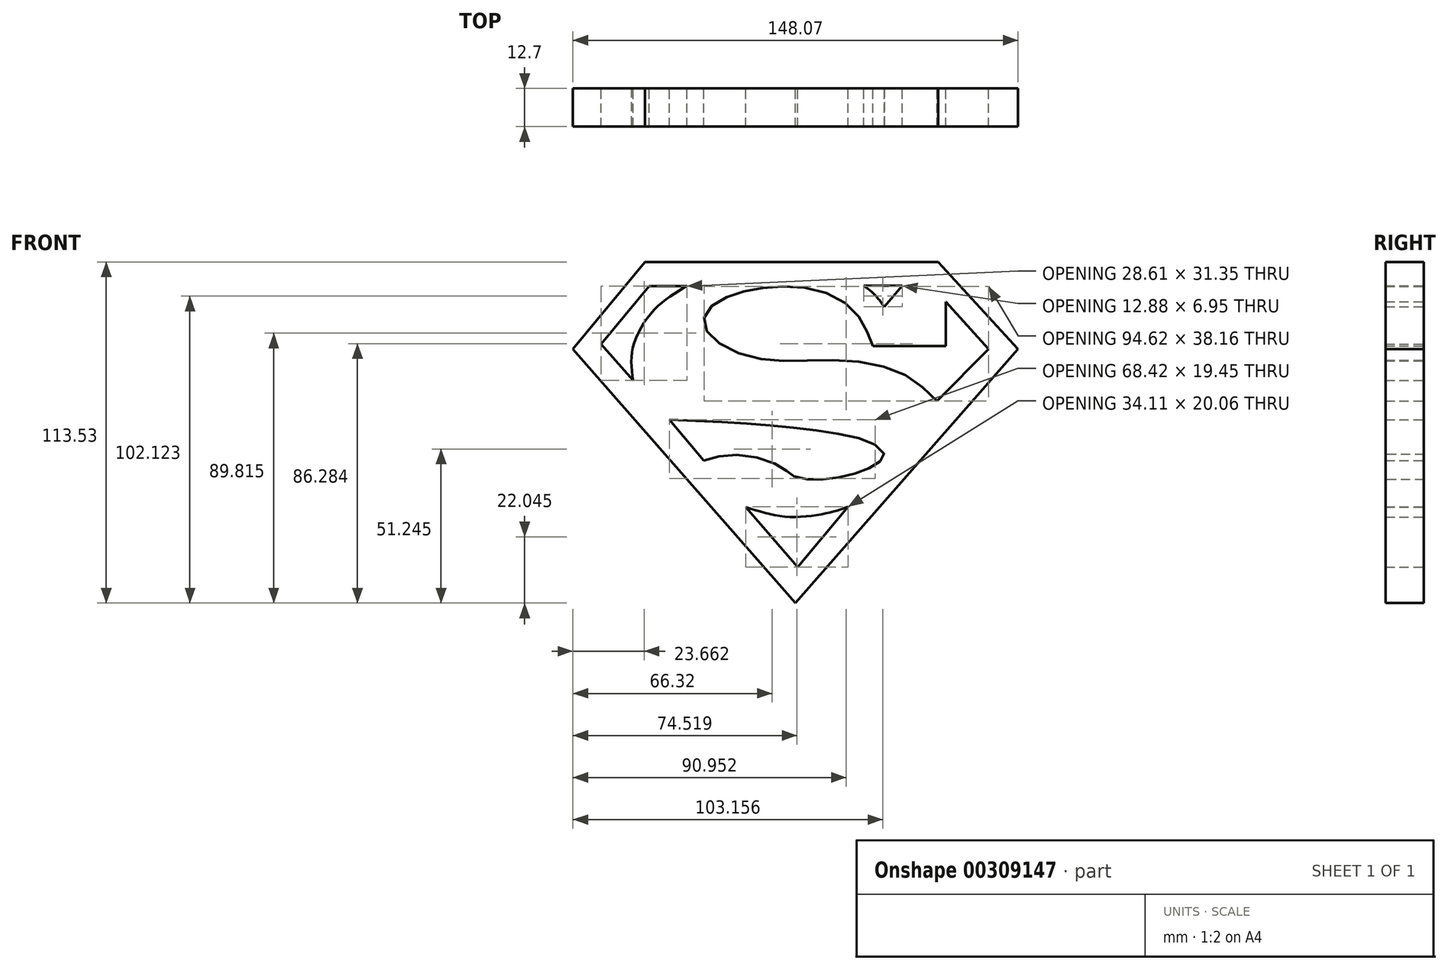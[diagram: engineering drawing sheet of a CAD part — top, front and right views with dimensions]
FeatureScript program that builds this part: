
annotation { "Feature Type Name" : "Feature", "Feature Type Description" : "" }
export const myFeature = defineFeature(function(context is Context, id is Id, definition is map)
    precondition{}
    {
        {
            var Q0;
            Q0=qCreatedBy(makeId("Front.planeOp"),FACE);
            var sketch = newSketch(context, id + "F0", { "sketchPlane" : qUnion([Q0])});
            skLineSegment(sketch, "E0", {"start": v(-48.05, 71.76) * mm, "end": v(-72.06, 42.8) * mm});
            skLineSegment(sketch, "E1", {"start": v(-72.06, 42.8) * mm, "end": v(1.98, -41.77) * mm});
            skLineSegment(sketch, "E2", {"start": v(1.98, -41.77) * mm, "end": v(76.01, 42.8) * mm});
            skLineSegment(sketch, "E3", {"start": v(76.01, 42.8) * mm, "end": v(49.52, 71.76) * mm});
            skLineSegment(sketch, "E4", {"start": v(49.52, 71.76) * mm, "end": v(-48.05, 71.76) * mm});
            skLineSegment(sketch, "E5", {"start": v(-46.67, 63.72) * mm, "end": v(-34.1, 63.72) * mm});
            skLineSegment(sketch, "E6", {"start": v(-46.67, 63.72) * mm, "end": v(-62.7, 44.39) * mm});
            skLineSegment(sketch, "E7", {"start": v(-62.7, 44.39) * mm, "end": v(-52.06, 32.37) * mm});
            skFitSpline(sketch, "E8", {"points": [v(-52.06, 32.37) * mm, v(-52.06, 43.51) * mm, v(-44.54, 56.3) * mm, v(-34.1, 63.72) * mm], "startDerivative": vector(-4.57, 35.12) * mm, "endDerivative": vector(32.68, 18.82) * mm});
            skLineSegment(sketch, "E9", {"start": v(24.66, 63.83) * mm, "end": v(37.54, 63.83) * mm});
            skLineSegment(sketch, "E10", {"start": v(37.54, 63.83) * mm, "end": v(31.5, 56.88) * mm});
            skFitSpline(sketch, "E11", {"points": [v(31.5, 56.88) * mm, v(28.1, 61.06) * mm, v(24.66, 63.83) * mm], "startDerivative": vector(-6.25, 8.53) * mm, "endDerivative": vector(-7.43, 5.31) * mm});
            skLineSegment(sketch, "E12", {"start": v(-14.6, -9.78) * mm, "end": v(2.67, -29.75) * mm});
            skLineSegment(sketch, "E13", {"start": v(2.67, -29.75) * mm, "end": v(19.51, -9.7) * mm});
            skFitSpline(sketch, "E14", {"points": [v(-14.6, -9.78) * mm, v(0, -13.08) * mm, v(14.27, -11.39) * mm, v(19.51, -9.7) * mm], "startDerivative": vector(36.48, -11.86) * mm, "endDerivative": vector(19.2, 7.11) * mm});
            skLineSegment(sketch, "E15", {"start": v(-39.95, 19.2) * mm, "end": v(-28.58, 5.61) * mm});
            skFitSpline(sketch, "E16", {"points": [v(-28.58, 5.61) * mm, v(-19.9, 7.59) * mm, v(-7.16, 5.61) * mm, v(-0.81, 2.14) * mm, v(1.34, 0.53) * mm, v(7.75, -0.67) * mm, v(16, 0) * mm, v(24.38, 2.2) * mm, v(29.7, 5.08) * mm, v(31.56, 7.35) * mm, v(28.45, 10.88) * mm, v(17.26, 14.41) * mm, v(0.68, 16.69) * mm, v(-17.75, 18.18) * mm, v(-39.95, 19.2) * mm], "startDerivative": vector(113.44, 37.94) * mm, "endDerivative": vector(-203.13, 7.97) * mm});
            skLineSegment(sketch, "E17", {"start": v(52.03, 43.75) * mm, "end": v(52.03, 58.53) * mm});
            skLineSegment(sketch, "E18", {"start": v(52.03, 58.53) * mm, "end": v(66.2, 42.7) * mm});
            skLineSegment(sketch, "E19", {"start": v(66.2, 42.7) * mm, "end": v(49.01, 25.43) * mm});
            skLineSegment(sketch, "E20", {"start": v(52.03, 43.75) * mm, "end": v(27.75, 43.75) * mm});
            skFitSpline(sketch, "E21", {"points": [v(49.01, 25.43) * mm, v(39.74, 33.42) * mm, v(23.3, 38.48) * mm, v(3.78, 38.93) * mm, v(-11.75, 39.83) * mm, v(-24.65, 45.64) * mm, v(-28.52, 51.66) * mm, v(-26.42, 56.61) * mm, v(-18.7, 60.84) * mm, v(-8.62, 63.06) * mm, v(4.61, 63.26) * mm, v(17.98, 58.53) * mm, v(24.9, 50.5) * mm, v(27.75, 43.75) * mm], "startDerivative": vector(-104.78, 109.8) * mm, "endDerivative": vector(38.9, -108.3) * mm});
            skSolve(sketch);
        }
        {
            var Q0;
            Q0=makeQuery(id+"F0.imprint","IMPRINT",FACE,{"disambiguationData":[TD([[makeQuery(id+"F0.imprint","IMPRINT",EDGE,{"derivedFrom":sQuery(id+"F0.wireOp",EDGE,"E0")}),1.0]])]});
            extrude(context, id + "F1", {"entities" : qUnion([Q0]), "depth" : 12.7 * mm});
        }
    });
